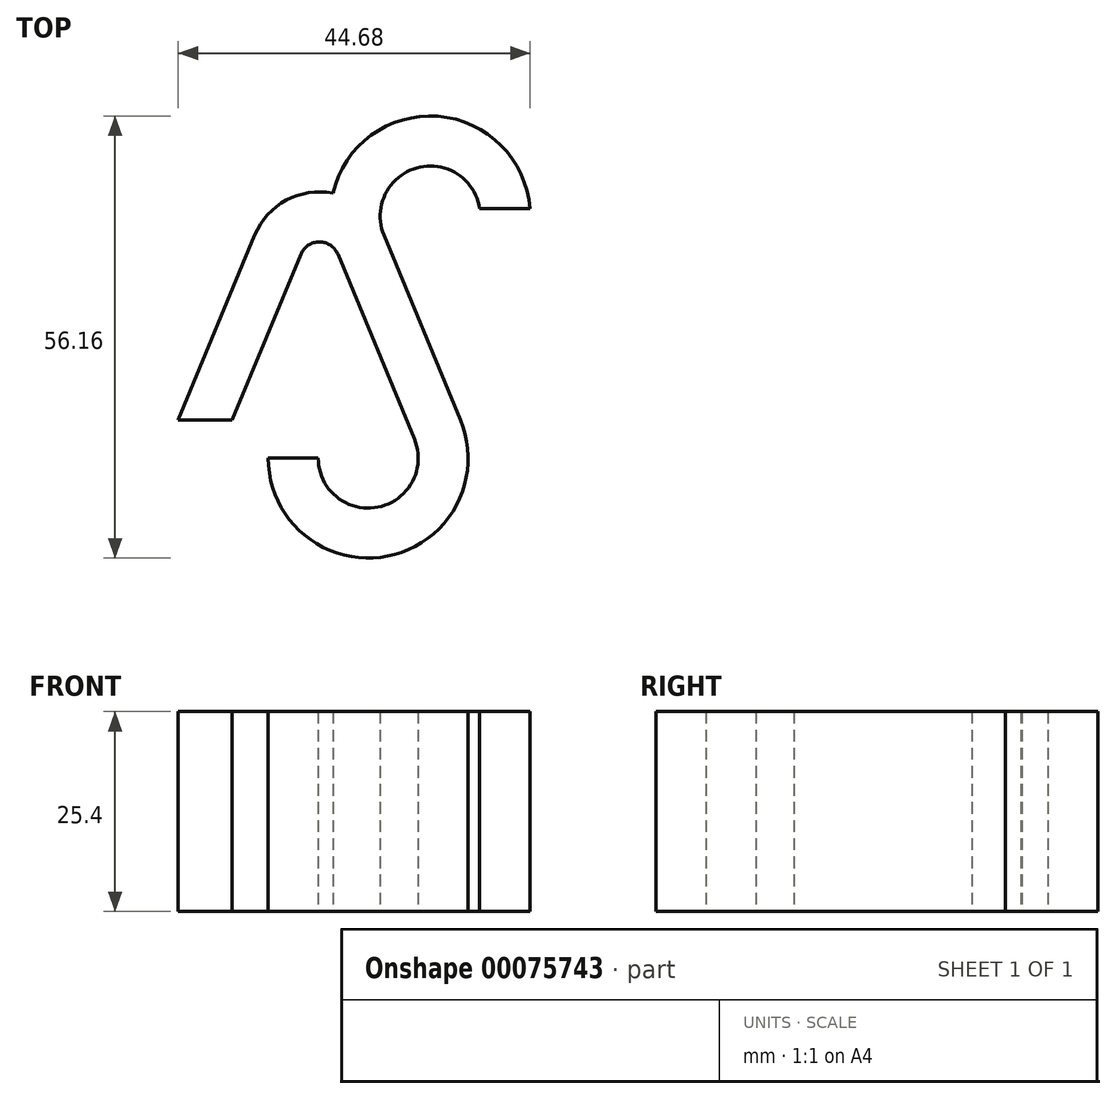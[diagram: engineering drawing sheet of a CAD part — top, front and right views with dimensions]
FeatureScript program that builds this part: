
annotation { "Feature Type Name" : "Feature", "Feature Type Description" : "" }
export const myFeature = defineFeature(function(context is Context, id is Id, definition is map)
    precondition{}
    {
        {
            var Q0;
            Q0=qCreatedBy(makeId("Top.planeOp"),FACE);
            var sketch = newSketch(context, id + "F0", { "sketchPlane" : qUnion([Q0])});
            skLineSegment(sketch, "E0", {"start": v(-39.76, -5.74) * mm, "end": v(-30.04, 17.73) * mm});
            skLineSegment(sketch, "E1", {"start": v(-13.61, 17.73) * mm, "end": v(-3.9, -5.74) * mm});
            skArc(sketch, "E2", {"start": v(-30.04, 17.73) * mm, "mid": v(-26.03, 22.16) * mm, "end": v(-20.11, 23.05) * mm});
            skLineSegment(sketch, "E3", {"start": v(-32.89, -5.74) * mm, "end": v(-24.17, 15.3) * mm});
            skLineSegment(sketch, "E4", {"start": v(-19.48, 15.3) * mm, "end": v(-9.76, -8.17) * mm});
            skArc(sketch, "E5", {"start": v(-24.17, 15.3) * mm, "mid": v(-21.83, 16.86) * mm, "end": v(-19.48, 15.3) * mm});
            skArc(sketch, "E6", {"start": v(-9.76, -8.17) * mm, "mid": v(-14.39, -16.83) * mm, "end": v(-21.98, -10.6) * mm});
            skArc(sketch, "E7", {"start": v(-3.9, -5.74) * mm, "mid": v(-13.15, -23.06) * mm, "end": v(-28.33, -10.6) * mm});
            skLineSegment(sketch, "E8", {"start": v(-32.89, -5.74) * mm, "end": v(-39.76, -5.74) * mm});
            skLineSegment(sketch, "E9", {"start": v(-21.98, -10.6) * mm, "end": v(-28.33, -10.6) * mm});
            skArc(sketch, "E10", {"start": v(4.92, 21.11) * mm, "mid": v(-6.77, 32.82) * mm, "end": v(-20.11, 23.05) * mm});
            skArc(sketch, "E11", {"start": v(-1.47, 21.11) * mm, "mid": v(-9.45, 26.27) * mm, "end": v(-13.61, 17.73) * mm});
            skLineSegment(sketch, "E12", {"start": v(-1.47, 21.11) * mm, "end": v(4.92, 21.11) * mm});
            skSolve(sketch);
        }
        {
            var Q0;
            Q0=makeQuery(id+"F0.imprint","IMPRINT",FACE,{"disambiguationData":[TD([[makeQuery(id+"F0.imprint","IMPRINT",EDGE,{"derivedFrom":sQuery(id+"F0.wireOp",EDGE,"E0")}),-1.0]])]});
            extrude(context, id + "F1", {"entities" : qUnion([Q0]), "depth" : 25.4 * mm});
        }
    });
